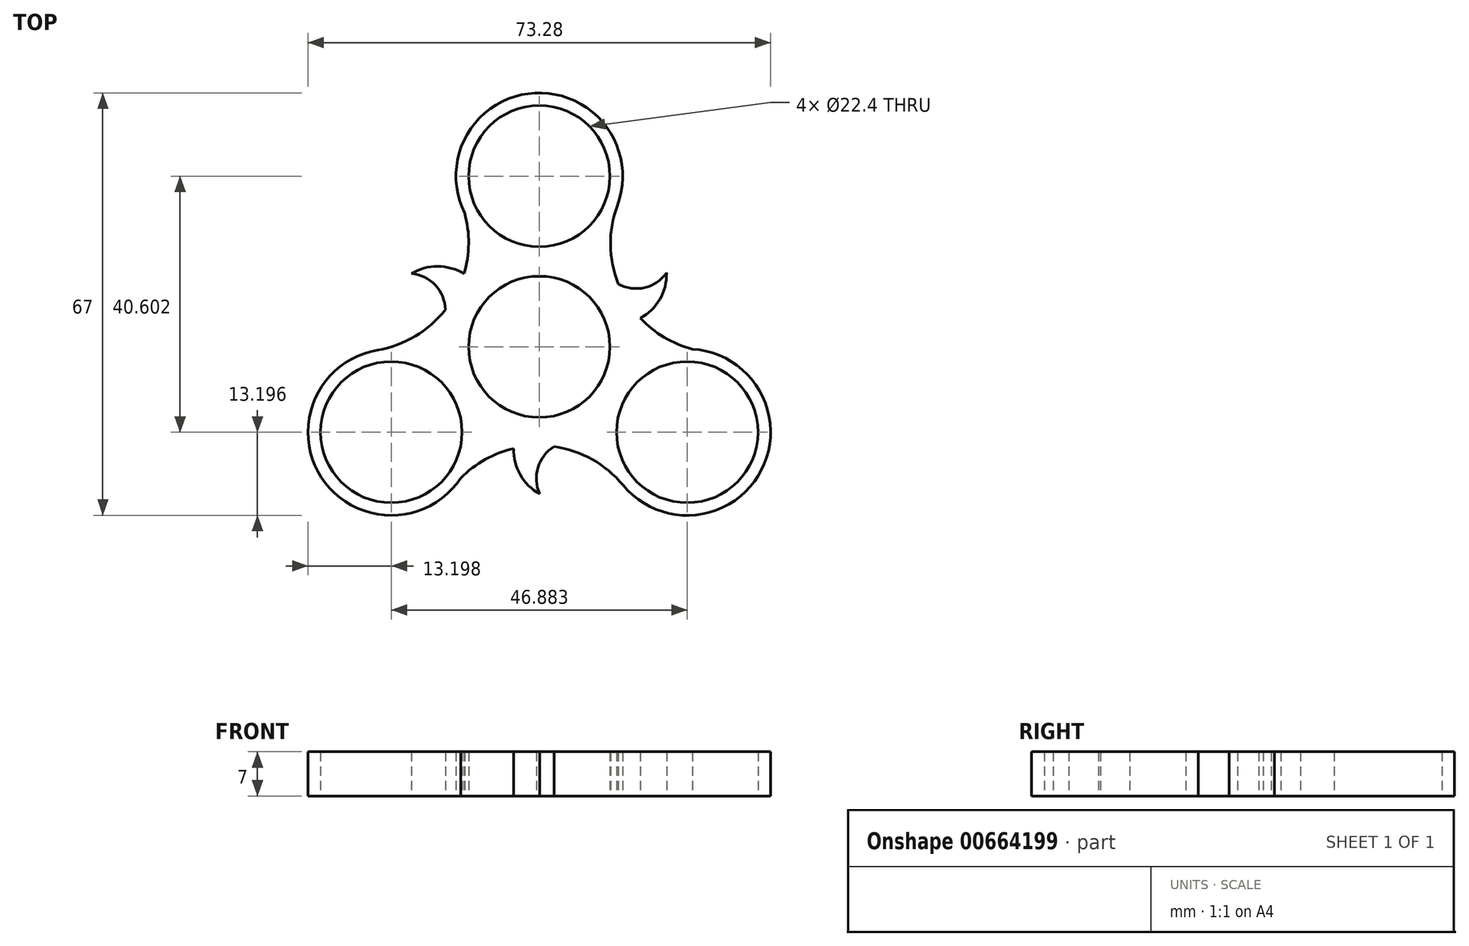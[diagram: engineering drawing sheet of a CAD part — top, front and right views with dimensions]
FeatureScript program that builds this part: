
annotation { "Feature Type Name" : "Feature", "Feature Type Description" : "" }
export const myFeature = defineFeature(function(context is Context, id is Id, definition is map)
    precondition{}
    {
        {
            var Q0;
            Q0=qCreatedBy(makeId("Top.planeOp"),FACE);
            var sketch = newSketch(context, id + "F0", { "sketchPlane" : qUnion([Q0])});
            skCircle(sketch, "E0", {"center": v(0, 0) * mm, "radius": 11.2 * mm});
            skCircle(sketch, "E1", {"center": v(0, 27.07) * mm, "radius": 11.2 * mm});
            skArc(sketch, "E2", {"start": v(12.36, 22.44) * mm, "mid": v(-0.69, 40.25) * mm, "end": v(-11.81, 21.18) * mm});
            skArc(sketch, "E3.1.0", {"start": v(-25.61, -0.51) * mm, "mid": v(-34.51, -20.72) * mm, "end": v(-12.43, -20.82) * mm});
            skCircle(sketch, "E3.1.1", {"center": v(-23.44, -13.53) * mm, "radius": 11.2 * mm});
            skArc(sketch, "E3.2.0", {"start": v(13.25, -21.92) * mm, "mid": v(35.2, -19.53) * mm, "end": v(24.25, -0.36) * mm});
            skCircle(sketch, "E3.2.1", {"center": v(23.44, -13.53) * mm, "radius": 11.2 * mm});
            skArc(sketch, "E4", {"start": v(12.36, 22.44) * mm, "mid": v(11.28, 16.18) * mm, "end": v(12.54, 9.95) * mm});
            skArc(sketch, "E5.1.0", {"start": v(-25.61, -0.51) * mm, "mid": v(-19.65, 1.68) * mm, "end": v(-14.88, 5.88) * mm});
            skArc(sketch, "E5.2.0", {"start": v(13.25, -21.92) * mm, "mid": v(8.37, -17.86) * mm, "end": v(2.35, -15.83) * mm});
            skArc(sketch, "E6", {"start": v(12.54, 9.95) * mm, "mid": v(16.69, 9.39) * mm, "end": v(20.17, 11.73) * mm});
            skArc(sketch, "E7", {"start": v(16, 4.54) * mm, "mid": v(19.09, 7.55) * mm, "end": v(20.17, 11.73) * mm});
            skArc(sketch, "E8.1.0", {"start": v(-14.88, 5.88) * mm, "mid": v(-16.47, 9.76) * mm, "end": v(-20.24, 11.6) * mm});
            skArc(sketch, "E8.1.1", {"start": v(-11.93, 11.58) * mm, "mid": v(-16.08, 12.76) * mm, "end": v(-20.24, 11.6) * mm});
            skArc(sketch, "E8.2.0", {"start": v(2.35, -15.83) * mm, "mid": v(-0.22, -19.15) * mm, "end": v(0.07, -23.33) * mm});
            skArc(sketch, "E8.2.1", {"start": v(-4.07, -16.12) * mm, "mid": v(-3, -20.3) * mm, "end": v(0.07, -23.33) * mm});
            skArc(sketch, "E9.trimOffspring", {"start": v(16, 4.54) * mm, "mid": v(19.78, 1.5) * mm, "end": v(24.25, -0.36) * mm});
            skArc(sketch, "E10.trimOffspring", {"start": v(-11.93, 11.58) * mm, "mid": v(-11.2, 16.37) * mm, "end": v(-11.81, 21.18) * mm});
            skArc(sketch, "E11.trimOffspring", {"start": v(-4.07, -16.12) * mm, "mid": v(-8.58, -17.88) * mm, "end": v(-12.43, -20.82) * mm});
            skSolve(sketch);
        }
        {
            var Q0;
            Q0=makeQuery(id+"F0.imprint","IMPRINT",FACE,{"disambiguationData":[TD([[makeQuery(id+"F0.imprint","IMPRINT",EDGE,{"derivedFrom":sQuery(id+"F0.wireOp",EDGE,"E0")}),-1.0]])]});
            extrude(context, id + "F1", {"entities" : qUnion([Q0]), "depth" : 7 * mm, "offsetDistance" : 25 * mm});
        }
    });
